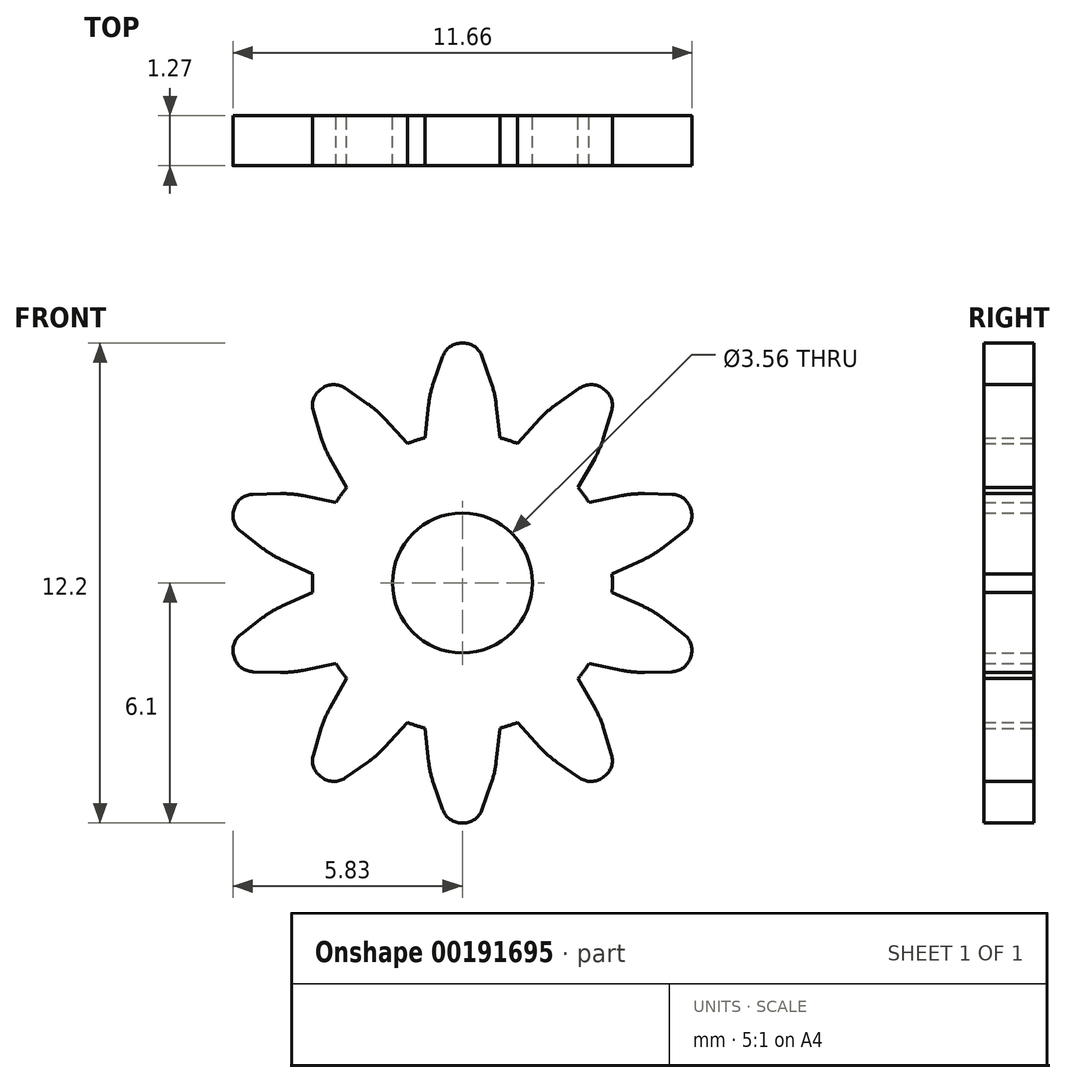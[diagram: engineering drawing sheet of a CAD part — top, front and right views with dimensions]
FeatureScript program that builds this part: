
annotation { "Feature Type Name" : "Feature", "Feature Type Description" : "" }
export const myFeature = defineFeature(function(context is Context, id is Id, definition is map)
    precondition{}
    {
        {
            var Q0;
            Q0=qCreatedBy(makeId("Front.planeOp"),FACE);
            var sketch = newSketch(context, id + "F0", { "sketchPlane" : qUnion([Q0])});
            skCircle(sketch, "E0", {"center": v(0, 0) * mm, "radius": 7.62 * mm});
            skLineSegment(sketch, "E1", {"start": v(-1.9, 7.38) * mm, "end": v(-0.76, 12.2) * mm, "construction": true});
            skLineSegment(sketch, "E2", {"start": v(-0.76, 12.2) * mm, "end": v(0.76, 12.2) * mm});
            skLineSegment(sketch, "E3", {"start": v(0.76, 12.2) * mm, "end": v(1.9, 7.38) * mm, "construction": true});
            skLineSegment(sketch, "E4", {"start": v(-1.9, 7.38) * mm, "end": v(-1.65, 9.65) * mm});
            skPoint(sketch, "E4.endSnap0", {"position": v(-1.33, 9.79) * mm});
            skLineSegment(sketch, "E5", {"start": v(-1.65, 9.65) * mm, "end": v(-0.76, 12.2) * mm});
            skLineSegment(sketch, "E6", {"start": v(1.9, 7.38) * mm, "end": v(1.65, 9.65) * mm});
            skPoint(sketch, "E6.endSnap0", {"position": v(1.33, 9.79) * mm});
            skLineSegment(sketch, "E7", {"start": v(1.65, 9.65) * mm, "end": v(0.76, 12.2) * mm});
            skLineSegment(sketch, "E8.1.0", {"start": v(-7.78, 9.42) * mm, "end": v(-6.55, 10.31) * mm});
            skLineSegment(sketch, "E8.1.1", {"start": v(-4.34, 8.78) * mm, "end": v(-6.55, 10.31) * mm});
            skLineSegment(sketch, "E8.1.2", {"start": v(-2.8, 7.09) * mm, "end": v(-4.34, 8.78) * mm});
            skLineSegment(sketch, "E8.1.3", {"start": v(-7, 6.84) * mm, "end": v(-7.78, 9.42) * mm});
            skLineSegment(sketch, "E8.1.4", {"start": v(-5.88, 4.85) * mm, "end": v(-7, 6.84) * mm});
            skLineSegment(sketch, "E8.2.0", {"start": v(-11.83, 3.04) * mm, "end": v(-11.36, 4.5) * mm});
            skLineSegment(sketch, "E8.2.1", {"start": v(-8.67, 4.55) * mm, "end": v(-11.36, 4.5) * mm});
            skLineSegment(sketch, "E8.2.2", {"start": v(-6.43, 4.1) * mm, "end": v(-8.67, 4.55) * mm});
            skLineSegment(sketch, "E8.2.3", {"start": v(-9.69, 1.41) * mm, "end": v(-11.83, 3.04) * mm});
            skLineSegment(sketch, "E8.2.4", {"start": v(-7.6, 0.47) * mm, "end": v(-9.69, 1.41) * mm});
            skLineSegment(sketch, "E8.3.0", {"start": v(-11.36, -4.5) * mm, "end": v(-11.83, -3.04) * mm});
            skLineSegment(sketch, "E8.3.1", {"start": v(-9.69, -1.41) * mm, "end": v(-11.83, -3.04) * mm});
            skLineSegment(sketch, "E8.3.2", {"start": v(-7.6, -0.47) * mm, "end": v(-9.69, -1.41) * mm});
            skLineSegment(sketch, "E8.3.3", {"start": v(-8.67, -4.55) * mm, "end": v(-11.36, -4.5) * mm});
            skLineSegment(sketch, "E8.3.4", {"start": v(-6.43, -4.1) * mm, "end": v(-8.67, -4.55) * mm});
            skLineSegment(sketch, "E8.4.0", {"start": v(-6.55, -10.31) * mm, "end": v(-7.78, -9.42) * mm});
            skLineSegment(sketch, "E8.4.1", {"start": v(-7, -6.84) * mm, "end": v(-7.78, -9.42) * mm});
            skLineSegment(sketch, "E8.4.2", {"start": v(-5.88, -4.85) * mm, "end": v(-7, -6.84) * mm});
            skLineSegment(sketch, "E8.4.3", {"start": v(-4.34, -8.78) * mm, "end": v(-6.55, -10.31) * mm});
            skLineSegment(sketch, "E8.4.4", {"start": v(-2.8, -7.09) * mm, "end": v(-4.34, -8.78) * mm});
            skLineSegment(sketch, "E8.5.0", {"start": v(0.76, -12.2) * mm, "end": v(-0.76, -12.2) * mm});
            skLineSegment(sketch, "E8.5.1", {"start": v(-1.65, -9.65) * mm, "end": v(-0.76, -12.2) * mm});
            skLineSegment(sketch, "E8.5.2", {"start": v(-1.9, -7.38) * mm, "end": v(-1.65, -9.65) * mm});
            skLineSegment(sketch, "E8.5.3", {"start": v(1.65, -9.65) * mm, "end": v(0.76, -12.2) * mm});
            skLineSegment(sketch, "E8.5.4", {"start": v(1.9, -7.38) * mm, "end": v(1.65, -9.65) * mm});
            skLineSegment(sketch, "E8.6.0", {"start": v(7.78, -9.42) * mm, "end": v(6.55, -10.31) * mm});
            skLineSegment(sketch, "E8.6.1", {"start": v(4.34, -8.78) * mm, "end": v(6.55, -10.31) * mm});
            skLineSegment(sketch, "E8.6.2", {"start": v(2.8, -7.09) * mm, "end": v(4.34, -8.78) * mm});
            skLineSegment(sketch, "E8.6.3", {"start": v(7, -6.84) * mm, "end": v(7.78, -9.42) * mm});
            skLineSegment(sketch, "E8.6.4", {"start": v(5.88, -4.85) * mm, "end": v(7, -6.84) * mm});
            skLineSegment(sketch, "E8.7.0", {"start": v(11.83, -3.04) * mm, "end": v(11.36, -4.5) * mm});
            skLineSegment(sketch, "E8.7.1", {"start": v(8.67, -4.55) * mm, "end": v(11.36, -4.5) * mm});
            skLineSegment(sketch, "E8.7.2", {"start": v(6.43, -4.1) * mm, "end": v(8.67, -4.55) * mm});
            skLineSegment(sketch, "E8.7.3", {"start": v(9.69, -1.41) * mm, "end": v(11.83, -3.04) * mm});
            skLineSegment(sketch, "E8.7.4", {"start": v(7.6, -0.47) * mm, "end": v(9.69, -1.41) * mm});
            skLineSegment(sketch, "E8.8.0", {"start": v(11.36, 4.5) * mm, "end": v(11.83, 3.04) * mm});
            skLineSegment(sketch, "E8.8.1", {"start": v(9.69, 1.41) * mm, "end": v(11.83, 3.04) * mm});
            skLineSegment(sketch, "E8.8.2", {"start": v(7.6, 0.47) * mm, "end": v(9.69, 1.41) * mm});
            skLineSegment(sketch, "E8.8.3", {"start": v(8.67, 4.55) * mm, "end": v(11.36, 4.5) * mm});
            skLineSegment(sketch, "E8.8.4", {"start": v(6.43, 4.1) * mm, "end": v(8.67, 4.55) * mm});
            skLineSegment(sketch, "E8.9.0", {"start": v(6.55, 10.31) * mm, "end": v(7.78, 9.42) * mm});
            skLineSegment(sketch, "E8.9.1", {"start": v(7, 6.84) * mm, "end": v(7.78, 9.42) * mm});
            skLineSegment(sketch, "E8.9.2", {"start": v(5.88, 4.85) * mm, "end": v(7, 6.84) * mm});
            skLineSegment(sketch, "E8.9.3", {"start": v(4.34, 8.78) * mm, "end": v(6.55, 10.31) * mm});
            skLineSegment(sketch, "E8.9.4", {"start": v(2.8, 7.09) * mm, "end": v(4.34, 8.78) * mm});
            skCircle(sketch, "E9", {"center": v(0, 0) * mm, "radius": 3.56 * mm});
            skSolve(sketch);
        }
        {
            var Q0;
            Q0=qSketchRegion(id+"F0",true);
            extrude(context, id + "F1", {"entities" : qUnion([Q0]), "depth" : 2.54 * mm});
        }
        {
            var Q0;
            Q0=makeQuery(id+"F1.opExtrude","SWEPT_EDGE",EDGE,{"disambiguationData":[OSD([sQuery(id+"F0.wireOp",EDGE,"E8.9.1"),sQuery(id+"F0.wireOp",EDGE,"E8.9.2")])]});
            var Q1;
            Q1=makeQuery(id+"F1.opExtrude","SWEPT_EDGE",EDGE,{"disambiguationData":[OSD([sQuery(id+"F0.wireOp",EDGE,"E8.9.3"),sQuery(id+"F0.wireOp",EDGE,"E8.9.4")])]});
            var Q2;
            Q2=makeQuery(id+"F1.opExtrude","SWEPT_EDGE",EDGE,{"disambiguationData":[OSD([sQuery(id+"F0.wireOp",EDGE,"E6"),sQuery(id+"F0.wireOp",EDGE,"E7")])]});
            var Q3;
            Q3=makeQuery(id+"F1.opExtrude","SWEPT_EDGE",EDGE,{"disambiguationData":[OSD([sQuery(id+"F0.wireOp",EDGE,"E8.1.1"),sQuery(id+"F0.wireOp",EDGE,"E8.1.2")])]});
            var Q4;
            Q4=makeQuery(id+"F1.opExtrude","SWEPT_EDGE",EDGE,{"disambiguationData":[OSD([sQuery(id+"F0.wireOp",EDGE,"E8.2.1"),sQuery(id+"F0.wireOp",EDGE,"E8.2.2")])]});
            var Q5;
            Q5=makeQuery(id+"F1.opExtrude","SWEPT_EDGE",EDGE,{"disambiguationData":[OSD([sQuery(id+"F0.wireOp",EDGE,"E8.3.1"),sQuery(id+"F0.wireOp",EDGE,"E8.3.2")])]});
            var Q6;
            Q6=makeQuery(id+"F1.opExtrude","SWEPT_EDGE",EDGE,{"disambiguationData":[OSD([sQuery(id+"F0.wireOp",EDGE,"E8.4.1"),sQuery(id+"F0.wireOp",EDGE,"E8.4.2")])]});
            var Q7;
            Q7=makeQuery(id+"F1.opExtrude","SWEPT_EDGE",EDGE,{"disambiguationData":[OSD([sQuery(id+"F0.wireOp",EDGE,"E8.5.1"),sQuery(id+"F0.wireOp",EDGE,"E8.5.2")])]});
            var Q8;
            Q8=makeQuery(id+"F1.opExtrude","SWEPT_EDGE",EDGE,{"disambiguationData":[OSD([sQuery(id+"F0.wireOp",EDGE,"E8.6.1"),sQuery(id+"F0.wireOp",EDGE,"E8.6.2")])]});
            var Q9;
            Q9=makeQuery(id+"F1.opExtrude","SWEPT_EDGE",EDGE,{"disambiguationData":[OSD([sQuery(id+"F0.wireOp",EDGE,"E8.7.1"),sQuery(id+"F0.wireOp",EDGE,"E8.7.2")])]});
            var Q10;
            Q10=makeQuery(id+"F1.opExtrude","SWEPT_EDGE",EDGE,{"disambiguationData":[OSD([sQuery(id+"F0.wireOp",EDGE,"E8.8.1"),sQuery(id+"F0.wireOp",EDGE,"E8.8.2")])]});
            var Q11;
            Q11=makeQuery(id+"F1.opExtrude","SWEPT_EDGE",EDGE,{"disambiguationData":[OSD([sQuery(id+"F0.wireOp",EDGE,"E8.7.3"),sQuery(id+"F0.wireOp",EDGE,"E8.7.4")])]});
            var Q12;
            Q12=makeQuery(id+"F1.opExtrude","SWEPT_EDGE",EDGE,{"disambiguationData":[OSD([sQuery(id+"F0.wireOp",EDGE,"E8.8.3"),sQuery(id+"F0.wireOp",EDGE,"E8.8.4")])]});
            var Q13;
            Q13=makeQuery(id+"F1.opExtrude","SWEPT_EDGE",EDGE,{"disambiguationData":[OSD([sQuery(id+"F0.wireOp",EDGE,"E4"),sQuery(id+"F0.wireOp",EDGE,"E5")])]});
            var Q14;
            Q14=makeQuery(id+"F1.opExtrude","SWEPT_EDGE",EDGE,{"disambiguationData":[OSD([sQuery(id+"F0.wireOp",EDGE,"E8.1.3"),sQuery(id+"F0.wireOp",EDGE,"E8.1.4")])]});
            var Q15;
            Q15=makeQuery(id+"F1.opExtrude","SWEPT_EDGE",EDGE,{"disambiguationData":[OSD([sQuery(id+"F0.wireOp",EDGE,"E8.2.3"),sQuery(id+"F0.wireOp",EDGE,"E8.2.4")])]});
            var Q16;
            Q16=makeQuery(id+"F1.opExtrude","SWEPT_EDGE",EDGE,{"disambiguationData":[OSD([sQuery(id+"F0.wireOp",EDGE,"E8.3.3"),sQuery(id+"F0.wireOp",EDGE,"E8.3.4")])]});
            var Q17;
            Q17=makeQuery(id+"F1.opExtrude","SWEPT_EDGE",EDGE,{"disambiguationData":[OSD([sQuery(id+"F0.wireOp",EDGE,"E8.4.3"),sQuery(id+"F0.wireOp",EDGE,"E8.4.4")])]});
            var Q18;
            Q18=makeQuery(id+"F1.opExtrude","SWEPT_EDGE",EDGE,{"disambiguationData":[OSD([sQuery(id+"F0.wireOp",EDGE,"E8.5.3"),sQuery(id+"F0.wireOp",EDGE,"E8.5.4")])]});
            var Q19;
            Q19=makeQuery(id+"F1.opExtrude","SWEPT_EDGE",EDGE,{"disambiguationData":[OSD([sQuery(id+"F0.wireOp",EDGE,"E8.6.3"),sQuery(id+"F0.wireOp",EDGE,"E8.6.4")])]});
            fillet(context, id + "F2", {"entities" : qUnion([Q0, Q1, Q2, Q3, Q4, Q5, Q6, Q7, Q8, Q9, Q10, Q11, Q12, Q13, Q14, Q15, Q16, Q17, Q18, Q19]), "radius" : 5.08 * mm, "tangentPropagation" : true, "allowEdgeOverflow" : false});
        }
        {
            var Q0;
            Q0=makeQuery(id+"F1.opExtrude","SWEPT_EDGE",EDGE,{"disambiguationData":[OSD([sQuery(id+"F0.wireOp",EDGE,"E2"),sQuery(id+"F0.wireOp",EDGE,"E7")])]});
            var Q1;
            Q1=makeQuery(id+"F1.opExtrude","SWEPT_EDGE",EDGE,{"disambiguationData":[OSD([sQuery(id+"F0.wireOp",EDGE,"E2"),sQuery(id+"F0.wireOp",EDGE,"E5")])]});
            var Q2;
            Q2=makeQuery(id+"F1.opExtrude","SWEPT_EDGE",EDGE,{"disambiguationData":[OSD([sQuery(id+"F0.wireOp",EDGE,"E8.1.0"),sQuery(id+"F0.wireOp",EDGE,"E8.1.1")])]});
            var Q3;
            Q3=makeQuery(id+"F1.opExtrude","SWEPT_EDGE",EDGE,{"disambiguationData":[OSD([sQuery(id+"F0.wireOp",EDGE,"E8.1.0"),sQuery(id+"F0.wireOp",EDGE,"E8.1.3")])]});
            var Q4;
            Q4=makeQuery(id+"F1.opExtrude","SWEPT_EDGE",EDGE,{"disambiguationData":[OSD([sQuery(id+"F0.wireOp",EDGE,"E8.2.0"),sQuery(id+"F0.wireOp",EDGE,"E8.2.1")])]});
            var Q5;
            Q5=makeQuery(id+"F1.opExtrude","SWEPT_EDGE",EDGE,{"disambiguationData":[OSD([sQuery(id+"F0.wireOp",EDGE,"E8.9.0"),sQuery(id+"F0.wireOp",EDGE,"E8.9.3")])]});
            var Q6;
            Q6=makeQuery(id+"F1.opExtrude","SWEPT_EDGE",EDGE,{"disambiguationData":[OSD([sQuery(id+"F0.wireOp",EDGE,"E8.9.0"),sQuery(id+"F0.wireOp",EDGE,"E8.9.1")])]});
            var Q7;
            Q7=makeQuery(id+"F1.opExtrude","SWEPT_EDGE",EDGE,{"disambiguationData":[OSD([sQuery(id+"F0.wireOp",EDGE,"E8.8.0"),sQuery(id+"F0.wireOp",EDGE,"E8.8.3")])]});
            var Q8;
            Q8=makeQuery(id+"F1.opExtrude","SWEPT_EDGE",EDGE,{"disambiguationData":[OSD([sQuery(id+"F0.wireOp",EDGE,"E8.2.0"),sQuery(id+"F0.wireOp",EDGE,"E8.2.3")])]});
            var Q9;
            Q9=makeQuery(id+"F1.opExtrude","SWEPT_EDGE",EDGE,{"disambiguationData":[OSD([sQuery(id+"F0.wireOp",EDGE,"E8.3.0"),sQuery(id+"F0.wireOp",EDGE,"E8.3.1")])]});
            var Q10;
            Q10=makeQuery(id+"F1.opExtrude","SWEPT_EDGE",EDGE,{"disambiguationData":[OSD([sQuery(id+"F0.wireOp",EDGE,"E8.3.0"),sQuery(id+"F0.wireOp",EDGE,"E8.3.3")])]});
            var Q11;
            Q11=makeQuery(id+"F1.opExtrude","SWEPT_EDGE",EDGE,{"disambiguationData":[OSD([sQuery(id+"F0.wireOp",EDGE,"E8.4.0"),sQuery(id+"F0.wireOp",EDGE,"E8.4.1")])]});
            var Q12;
            Q12=makeQuery(id+"F1.opExtrude","SWEPT_EDGE",EDGE,{"disambiguationData":[OSD([sQuery(id+"F0.wireOp",EDGE,"E8.4.0"),sQuery(id+"F0.wireOp",EDGE,"E8.4.3")])]});
            var Q13;
            Q13=makeQuery(id+"F1.opExtrude","SWEPT_EDGE",EDGE,{"disambiguationData":[OSD([sQuery(id+"F0.wireOp",EDGE,"E8.5.0"),sQuery(id+"F0.wireOp",EDGE,"E8.5.1")])]});
            var Q14;
            Q14=makeQuery(id+"F1.opExtrude","SWEPT_EDGE",EDGE,{"disambiguationData":[OSD([sQuery(id+"F0.wireOp",EDGE,"E8.5.0"),sQuery(id+"F0.wireOp",EDGE,"E8.5.3")])]});
            var Q15;
            Q15=makeQuery(id+"F1.opExtrude","SWEPT_EDGE",EDGE,{"disambiguationData":[OSD([sQuery(id+"F0.wireOp",EDGE,"E8.6.0"),sQuery(id+"F0.wireOp",EDGE,"E8.6.1")])]});
            var Q16;
            Q16=makeQuery(id+"F1.opExtrude","SWEPT_EDGE",EDGE,{"disambiguationData":[OSD([sQuery(id+"F0.wireOp",EDGE,"E8.6.0"),sQuery(id+"F0.wireOp",EDGE,"E8.6.3")])]});
            var Q17;
            Q17=makeQuery(id+"F1.opExtrude","SWEPT_EDGE",EDGE,{"disambiguationData":[OSD([sQuery(id+"F0.wireOp",EDGE,"E8.7.0"),sQuery(id+"F0.wireOp",EDGE,"E8.7.3")])]});
            var Q18;
            Q18=makeQuery(id+"F1.opExtrude","SWEPT_EDGE",EDGE,{"disambiguationData":[OSD([sQuery(id+"F0.wireOp",EDGE,"E8.7.0"),sQuery(id+"F0.wireOp",EDGE,"E8.7.1")])]});
            var Q19;
            Q19=makeQuery(id+"F1.opExtrude","SWEPT_EDGE",EDGE,{"disambiguationData":[OSD([sQuery(id+"F0.wireOp",EDGE,"E8.8.0"),sQuery(id+"F0.wireOp",EDGE,"E8.8.1")])]});
            fillet(context, id + "F3", {"entities" : qUnion([Q0, Q1, Q2, Q3, Q4, Q5, Q6, Q7, Q8, Q9, Q10, Q11, Q12, Q13, Q14, Q15, Q16, Q17, Q18, Q19]), "radius" : 1.02 * mm, "tangentPropagation" : true, "allowEdgeOverflow" : false});
        }
        {
            var Q0;
            Q0=makeQuery(id+"F1.opExtrude","SWEPT_BODY",BODY,{"disambiguationData":[OSD([sQuery(id+"F0.wireOp",EDGE,"E0"),sQuery(id+"F0.wireOp",EDGE,"E2"),sQuery(id+"F0.wireOp",EDGE,"E4"),sQuery(id+"F0.wireOp",EDGE,"E5"),sQuery(id+"F0.wireOp",EDGE,"E6"),sQuery(id+"F0.wireOp",EDGE,"E7"),sQuery(id+"F0.wireOp",EDGE,"E8.1.0"),sQuery(id+"F0.wireOp",EDGE,"E8.1.1"),sQuery(id+"F0.wireOp",EDGE,"E8.1.2"),sQuery(id+"F0.wireOp",EDGE,"E8.1.3"),sQuery(id+"F0.wireOp",EDGE,"E8.1.4"),sQuery(id+"F0.wireOp",EDGE,"E8.2.0"),sQuery(id+"F0.wireOp",EDGE,"E8.2.1"),sQuery(id+"F0.wireOp",EDGE,"E8.2.2"),sQuery(id+"F0.wireOp",EDGE,"E8.2.3"),sQuery(id+"F0.wireOp",EDGE,"E8.2.4"),sQuery(id+"F0.wireOp",EDGE,"E8.3.0"),sQuery(id+"F0.wireOp",EDGE,"E8.3.1"),sQuery(id+"F0.wireOp",EDGE,"E8.3.2"),sQuery(id+"F0.wireOp",EDGE,"E8.3.3"),sQuery(id+"F0.wireOp",EDGE,"E8.3.4"),sQuery(id+"F0.wireOp",EDGE,"E8.4.0"),sQuery(id+"F0.wireOp",EDGE,"E8.4.1"),sQuery(id+"F0.wireOp",EDGE,"E8.4.2"),sQuery(id+"F0.wireOp",EDGE,"E8.4.3"),sQuery(id+"F0.wireOp",EDGE,"E8.4.4"),sQuery(id+"F0.wireOp",EDGE,"E8.5.0"),sQuery(id+"F0.wireOp",EDGE,"E8.5.1"),sQuery(id+"F0.wireOp",EDGE,"E8.5.2"),sQuery(id+"F0.wireOp",EDGE,"E8.5.3"),sQuery(id+"F0.wireOp",EDGE,"E8.5.4"),sQuery(id+"F0.wireOp",EDGE,"E8.6.0"),sQuery(id+"F0.wireOp",EDGE,"E8.6.1"),sQuery(id+"F0.wireOp",EDGE,"E8.6.2"),sQuery(id+"F0.wireOp",EDGE,"E8.6.3"),sQuery(id+"F0.wireOp",EDGE,"E8.6.4"),sQuery(id+"F0.wireOp",EDGE,"E8.7.0"),sQuery(id+"F0.wireOp",EDGE,"E8.7.1"),sQuery(id+"F0.wireOp",EDGE,"E8.7.2"),sQuery(id+"F0.wireOp",EDGE,"E8.7.3"),sQuery(id+"F0.wireOp",EDGE,"E8.7.4"),sQuery(id+"F0.wireOp",EDGE,"E8.8.0"),sQuery(id+"F0.wireOp",EDGE,"E8.8.1"),sQuery(id+"F0.wireOp",EDGE,"E8.8.2"),sQuery(id+"F0.wireOp",EDGE,"E8.8.3"),sQuery(id+"F0.wireOp",EDGE,"E8.8.4"),sQuery(id+"F0.wireOp",EDGE,"E8.9.0"),sQuery(id+"F0.wireOp",EDGE,"E8.9.1"),sQuery(id+"F0.wireOp",EDGE,"E8.9.2"),sQuery(id+"F0.wireOp",EDGE,"E8.9.3"),sQuery(id+"F0.wireOp",EDGE,"E8.9.4"),sQuery(id+"F0.wireOp",EDGE,"E9")])]});
            var Q1;
            Q1=qCreatedBy(makeId("Origin.pointOp"),VERTEX);
            transform(context, id + "F4", {"entities" : qUnion([Q0]), "transformType" : TransformType.SCALE_UNIFORMLY, "scale" : .5, "scalePoint" : qUnion([Q1]), "makeCopy" : false});
        }
    });
